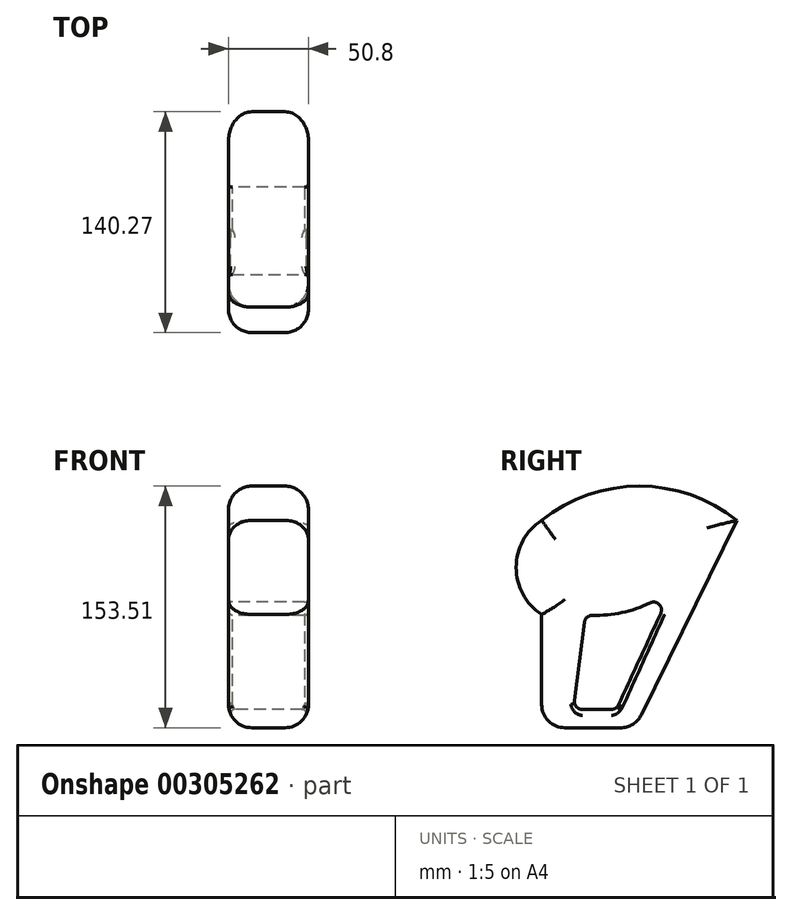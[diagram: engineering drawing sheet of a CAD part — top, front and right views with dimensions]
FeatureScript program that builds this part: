
annotation { "Feature Type Name" : "Feature", "Feature Type Description" : "" }
export const myFeature = defineFeature(function(context is Context, id is Id, definition is map)
    precondition{}
    {
        {
            var Q0;
            Q0=qCreatedBy(makeId("Right.planeOp"),FACE);
            var sketch = newSketch(context, id + "F0", { "sketchPlane" : qUnion([Q0])});
            skArc(sketch, "E0", {"start": v(76.55, 0) * mm, "mid": v(14.52, 21.77) * mm, "end": v(-47.5, 0) * mm});
            skArc(sketch, "E1", {"start": v(-47.5, 0) * mm, "mid": v(-63.72, -29.87) * mm, "end": v(-47.5, -59.75) * mm});
            skLineSegment(sketch, "E2.bottom", {"start": v(-47.5, -59.75) * mm, "end": v(11.83, -59.75) * mm});
            skLineSegment(sketch, "E2.top", {"start": v(-47.5, -131.74) * mm, "end": v(11.83, -131.74) * mm});
            skLineSegment(sketch, "E2.left", {"start": v(-47.5, -59.75) * mm, "end": v(-47.5, -131.74) * mm});
            skLineSegment(sketch, "E2.right", {"start": v(11.83, -59.75) * mm, "end": v(11.83, -131.74) * mm});
            skLineSegment(sketch, "E3", {"start": v(76.55, 0) * mm, "end": v(11.83, -131.74) * mm});
            skSolve(sketch);
        }
        {
            var Q0;
            Q0=makeQuery(id+"F0.imprint","IMPRINT",FACE,{"disambiguationData":[TD([[makeQuery(id+"F0.imprint","IMPRINT",EDGE,{"derivedFrom":sQuery(id+"F0.wireOp",EDGE,"E0")}),1.0]])]});
            var Q1;
            Q1=makeQuery(id+"F0.imprint","IMPRINT",FACE,{"disambiguationData":[TD([[makeQuery(id+"F0.imprint","IMPRINT",EDGE,{"derivedFrom":sQuery(id+"F0.wireOp",EDGE,"E2.bottom")}),-1.0]])]});
            extrude(context, id + "F1", {"entities" : qUnion([Q0, Q1]), "depth" : 25.4 * mm, "hasSecondDirection" : true, "secondDirectionOppositeDirection" : true, "secondDirectionDepth" : 25.4 * mm});
        }
        {
            var Q0;
            Q0=qCreatedBy(makeId("Right.planeOp"),FACE);
            var sketch = newSketch(context, id + "F2", { "sketchPlane" : qUnion([Q0])});
            skArc(sketch, "E4", {"start": v(-19.76, -60) * mm, "mid": v(9.3, -57.05) * mm, "end": v(35.25, -43.65) * mm});
            skLineSegment(sketch, "E5", {"start": v(35.25, -43.65) * mm, "end": v(0, -120.08) * mm});
            skLineSegment(sketch, "E6", {"start": v(0, -120.08) * mm, "end": v(-27.42, -120.08) * mm});
            skLineSegment(sketch, "E7", {"start": v(-27.42, -120.08) * mm, "end": v(-19.76, -60) * mm});
            skSolve(sketch);
        }
        {
            var Q0;
            Q0 = qSketchRegion(id + "F2", true);
            var Q1;
            Q1=sQuery(id+"F2.wireOp",EDGE,"E7");
            var Q2;
            Q2=sQuery(id+"F2.wireOp",EDGE,"E6");
            var Q3;
            Q3=sQuery(id+"F2.wireOp",EDGE,"E5");
            var Q4;
            Q4=sQuery(id+"F2.wireOp",EDGE,"E4");
            extrude(context, id + "F3", {"entities" : qUnion([Q0]), "operationType" : NewBodyOperationType.REMOVE, "surfaceEntities" : qUnion([Q1, Q2, Q3, Q4]), "endBound" : BoundingType.THROUGH_ALL, "depth" : 25.4 * mm, "hasSecondDirection" : true, "secondDirectionBound" : SecondDirectionBoundingType.THROUGH_ALL, "secondDirectionOppositeDirection" : true, "secondDirectionDepth" : 25.4 * mm});
        }
        {
            var Q0;
            Q0=makeQuery(id+"F1.opExtrude","CAP_EDGE",EDGE,{"disambiguationData":[OSD([sQuery(id+"F0.wireOp",EDGE,"E0")])],"isStart":false});
            var Q1;
            Q1=makeQuery(id+"F1.opExtrude","CAP_EDGE",EDGE,{"disambiguationData":[OSD([sQuery(id+"F0.wireOp",EDGE,"E0")])],"isStart":true});
            var Q2;
            Q2=makeQuery(id+"F1.opExtrude","CAP_EDGE",EDGE,{"disambiguationData":[OSD([sQuery(id+"F0.wireOp",EDGE,"E1")])],"isStart":false});
            var Q3;
            Q3=makeQuery(id+"F1.opExtrude","CAP_EDGE",EDGE,{"disambiguationData":[OSD([sQuery(id+"F0.wireOp",EDGE,"E1")])],"isStart":true});
            var Q4;
            Q4=makeQuery(id+"F1.opExtrude","SWEPT_EDGE",EDGE,{"disambiguationData":[OSD([sQuery(id+"F0.wireOp",EDGE,"E2.top"),sQuery(id+"F0.wireOp",EDGE,"E2.left")])]});
            var Q5;
            Q5=makeQuery(id+"F1.opExtrude","CAP_EDGE",EDGE,{"disambiguationData":[OSD([sQuery(id+"F0.wireOp",EDGE,"E2.top")])],"isStart":false});
            var Q6;
            Q6=makeQuery(id+"F1.opExtrude","SWEPT_EDGE",EDGE,{"disambiguationData":[OSD([sQuery(id+"F0.wireOp",EDGE,"E2.top"),sQuery(id+"F0.wireOp",EDGE,"E2.right"),sQuery(id+"F0.wireOp",EDGE,"E3")])]});
            var Q7;
            Q7=makeQuery(id+"F1.opExtrude","CAP_EDGE",EDGE,{"disambiguationData":[OSD([sQuery(id+"F0.wireOp",EDGE,"E2.top")])],"isStart":true});
            var Q8;
            Q8=makeQuery(id+"F1.opExtrude","CAP_EDGE",EDGE,{"disambiguationData":[OSD([sQuery(id+"F0.wireOp",EDGE,"E2.left")])],"isStart":false});
            var Q9;
            Q9=makeQuery(id+"F1.opExtrude","CAP_EDGE",EDGE,{"disambiguationData":[OSD([sQuery(id+"F0.wireOp",EDGE,"E2.left")])],"isStart":true});
            var Q10;
            Q10=makeQuery(id+"F1.opExtrude","CAP_EDGE",EDGE,{"disambiguationData":[OSD([sQuery(id+"F0.wireOp",EDGE,"E3")])],"isStart":true});
            var Q11;
            Q11=makeQuery(id+"F1.opExtrude","CAP_EDGE",EDGE,{"disambiguationData":[OSD([sQuery(id+"F0.wireOp",EDGE,"E3")])],"isStart":false});
            fillet(context, id + "F4", {"entities" : qUnion([Q0, Q1, Q2, Q3, Q4, Q5, Q6, Q7, Q8, Q9, Q10, Q11]), "radius" : 14.86 * mm, "tangentPropagation" : true, "allowEdgeOverflow" : false});
        }
        {
            var Q0;
            Q0=makeQuery(id+"F3.boolean.opBoolean","COPY",EDGE,{"derivedFrom":makeQuery(id+"F3.opExtrude","SWEPT_EDGE",EDGE,{"disambiguationData":[OSD([sQuery(id+"F2.wireOp",EDGE,"E4"),sQuery(id+"F2.wireOp",EDGE,"E7")])]})});
            var Q1;
            Q1=makeQuery(id+"F3.boolean.opBoolean","COPY",EDGE,{"derivedFrom":makeQuery(id+"F3.opExtrude","SWEPT_EDGE",EDGE,{"disambiguationData":[OSD([sQuery(id+"F2.wireOp",EDGE,"E4"),sQuery(id+"F2.wireOp",EDGE,"E5")])]})});
            var Q2;
            Q2=makeQuery(id+"F3.boolean.opBoolean","COPY",EDGE,{"derivedFrom":makeQuery(id+"F3.opExtrude","SWEPT_EDGE",EDGE,{"disambiguationData":[OSD([sQuery(id+"F2.wireOp",EDGE,"E6"),sQuery(id+"F2.wireOp",EDGE,"E7")])]})});
            var Q3;
            Q3=makeQuery(id+"F3.boolean.opBoolean","COPY",EDGE,{"derivedFrom":makeQuery(id+"F3.opExtrude","SWEPT_EDGE",EDGE,{"disambiguationData":[OSD([sQuery(id+"F2.wireOp",EDGE,"E5"),sQuery(id+"F2.wireOp",EDGE,"E6")])]})});
            fillet(context, id + "F5", {"entities" : qUnion([Q0, Q1, Q2, Q3]), "radius" : 5.08 * mm, "tangentPropagation" : true, "allowEdgeOverflow" : false});
        }
        {
            var Q0;
            Q0=makeQuery(id+"F3.boolean.opBoolean","INTERSECT",EDGE,{"derivedFrom":[makeQuery(id+"F1.opExtrude","CAP_FACE",FACE,{"disambiguationData":[OSD([sQuery(id+"F0.wireOp",EDGE,"E0"),sQuery(id+"F0.wireOp",EDGE,"E1"),sQuery(id+"F0.wireOp",EDGE,"E2.top"),sQuery(id+"F0.wireOp",EDGE,"E2.left"),sQuery(id+"F0.wireOp",EDGE,"E3")])],"isStart":true}),makeQuery(id+"F3.opExtrude","SWEPT_FACE",FACE,{"disambiguationData":[OSD([sQuery(id+"F2.wireOp",EDGE,"E7")])]})]});
            var Q1;
            Q1=makeQuery(id+"F3.boolean.opBoolean","INTERSECT",EDGE,{"derivedFrom":[makeQuery(id+"F1.opExtrude","CAP_FACE",FACE,{"disambiguationData":[OSD([sQuery(id+"F0.wireOp",EDGE,"E0"),sQuery(id+"F0.wireOp",EDGE,"E1"),sQuery(id+"F0.wireOp",EDGE,"E2.top"),sQuery(id+"F0.wireOp",EDGE,"E2.left"),sQuery(id+"F0.wireOp",EDGE,"E3")])],"isStart":false}),makeQuery(id+"F3.opExtrude","SWEPT_FACE",FACE,{"disambiguationData":[OSD([sQuery(id+"F2.wireOp",EDGE,"E7")])]})]});
            fillet(context, id + "F6", {"entities" : qUnion([Q0, Q1]), "radius" : 2.54 * mm, "tangentPropagation" : true, "allowEdgeOverflow" : false});
        }
    });
